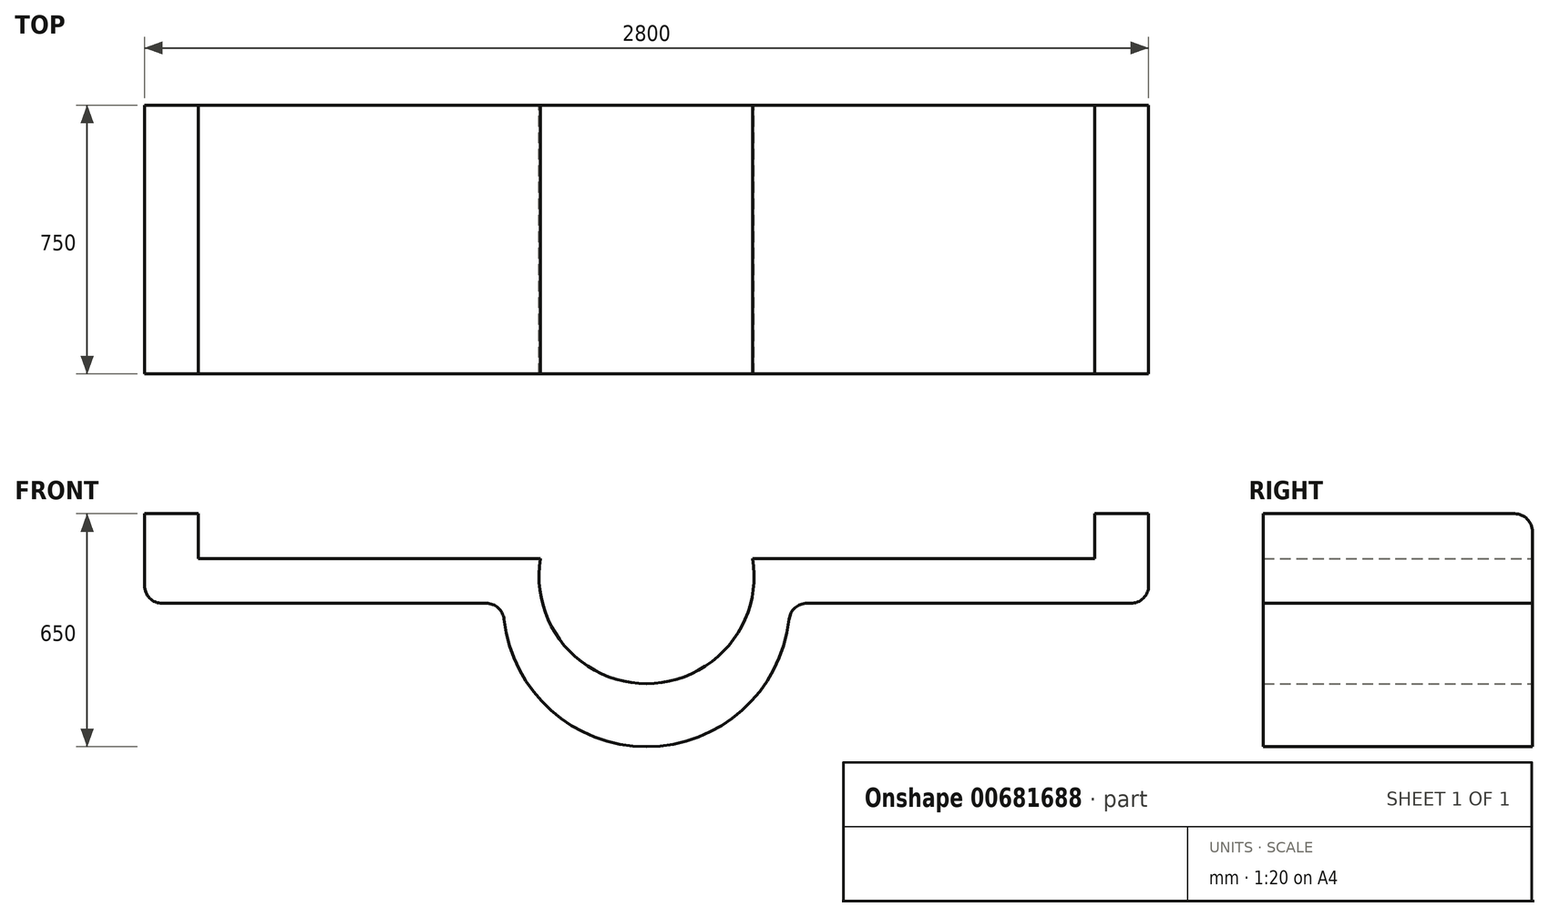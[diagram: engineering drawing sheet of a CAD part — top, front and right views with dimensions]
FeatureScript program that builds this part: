
annotation { "Feature Type Name" : "Feature", "Feature Type Description" : "" }
export const myFeature = defineFeature(function(context is Context, id is Id, definition is map)
    precondition{}
    {
        {
            var Q0;
            Q0=qCreatedBy(makeId("Front.planeOp"),FACE);
            var sketch = newSketch(context, id + "F0", { "sketchPlane" : qUnion([Q0])});
            skLineSegment(sketch, "E0", {"start": v(0, 0) * mm, "end": v(1000, 0) * mm});
            skLineSegment(sketch, "E1", {"start": v(1000, 0) * mm, "end": v(1000, 250) * mm});
            skLineSegment(sketch, "E2", {"start": v(1000, 250) * mm, "end": v(850, 250) * mm});
            skLineSegment(sketch, "E3", {"start": v(850, 250) * mm, "end": v(850, 125) * mm});
            skPoint(sketch, "E3.endSnap0", {"position": v(1000, 125) * mm});
            skLineSegment(sketch, "E4", {"start": v(850, 125) * mm, "end": v(-104.07, 125) * mm});
            skLineSegment(sketch, "E5", {"start": v(-800, 0) * mm, "end": v(-1800, 0) * mm});
            skLineSegment(sketch, "E6", {"start": v(-1800, 0) * mm, "end": v(-1800, 250) * mm});
            skLineSegment(sketch, "E7", {"start": v(-1800, 250) * mm, "end": v(-1650, 250) * mm});
            skLineSegment(sketch, "E8", {"start": v(-1650, 250) * mm, "end": v(-1650, 125) * mm});
            skPoint(sketch, "E8.endSnap0", {"position": v(-1800, 125) * mm});
            skLineSegment(sketch, "E9", {"start": v(-1650, 125) * mm, "end": v(-695.93, 125) * mm});
            skArc(sketch, "E10", {"start": v(-800, 0) * mm, "mid": v(-400, -400) * mm, "end": v(0, 0) * mm});
            skArc(sketch, "E11", {"start": v(-695.93, 125) * mm, "mid": v(-400, -224.25) * mm, "end": v(-104.07, 125) * mm});
            skSolve(sketch);
        }
        {
            var Q0;
            Q0 = qSketchRegion(id + "F0", true);
            extrude(context, id + "F1", {"entities" : qUnion([Q0]), "depth" : 750 * mm, "offsetDistance" : 25 * mm});
        }
        {
            var Q0;
            Q0=makeQuery(id+"F1.opExtrude","SWEPT_EDGE",EDGE,{"disambiguationData":[OSD([sQuery(id+"F0.wireOp",EDGE,"E0"),sQuery(id+"F0.wireOp",EDGE,"E1")])]});
            fillet(context, id + "F2", {"entities" : qUnion([Q0]), "radius" : 50 * mm, "tangentPropagation" : true, "allowEdgeOverflow" : false});
        }
        {
            var Q0;
            Q0=makeQuery(id+"F1.opExtrude","CAP_EDGE",EDGE,{"disambiguationData":[OSD([sQuery(id+"F0.wireOp",EDGE,"E2")])],"isStart":true});
            fillet(context, id + "F3", {"entities" : qUnion([Q0]), "radius" : 50 * mm, "tangentPropagation" : true, "allowEdgeOverflow" : false});
        }
        {
            var Q0;
            Q0=makeQuery(id+"F1.opExtrude","SWEPT_EDGE",EDGE,{"disambiguationData":[OSD([sQuery(id+"F0.wireOp",EDGE,"E0"),sQuery(id+"F0.wireOp",EDGE,"E10")])]});
            fillet(context, id + "F4", {"entities" : qUnion([Q0]), "radius" : 50 * mm, "tangentPropagation" : true, "allowEdgeOverflow" : false});
        }
        {
            var Q0;
            Q0=makeQuery(id+"F1.opExtrude","SWEPT_EDGE",EDGE,{"disambiguationData":[OSD([sQuery(id+"F0.wireOp",EDGE,"E5"),sQuery(id+"F0.wireOp",EDGE,"E10")])]});
            fillet(context, id + "F5", {"entities" : qUnion([Q0]), "radius" : 50 * mm, "tangentPropagation" : true, "allowEdgeOverflow" : false});
        }
        {
            var Q0;
            Q0=makeQuery(id+"F1.opExtrude","SWEPT_EDGE",EDGE,{"disambiguationData":[OSD([sQuery(id+"F0.wireOp",EDGE,"E5"),sQuery(id+"F0.wireOp",EDGE,"E6")])]});
            var Q1;
            Q1=makeQuery(id+"F1.opExtrude","CAP_EDGE",EDGE,{"disambiguationData":[OSD([sQuery(id+"F0.wireOp",EDGE,"E7")])],"isStart":true});
            fillet(context, id + "F6", {"entities" : qUnion([Q0, Q1]), "radius" : 50 * mm, "tangentPropagation" : true, "allowEdgeOverflow" : false});
        }
    });
